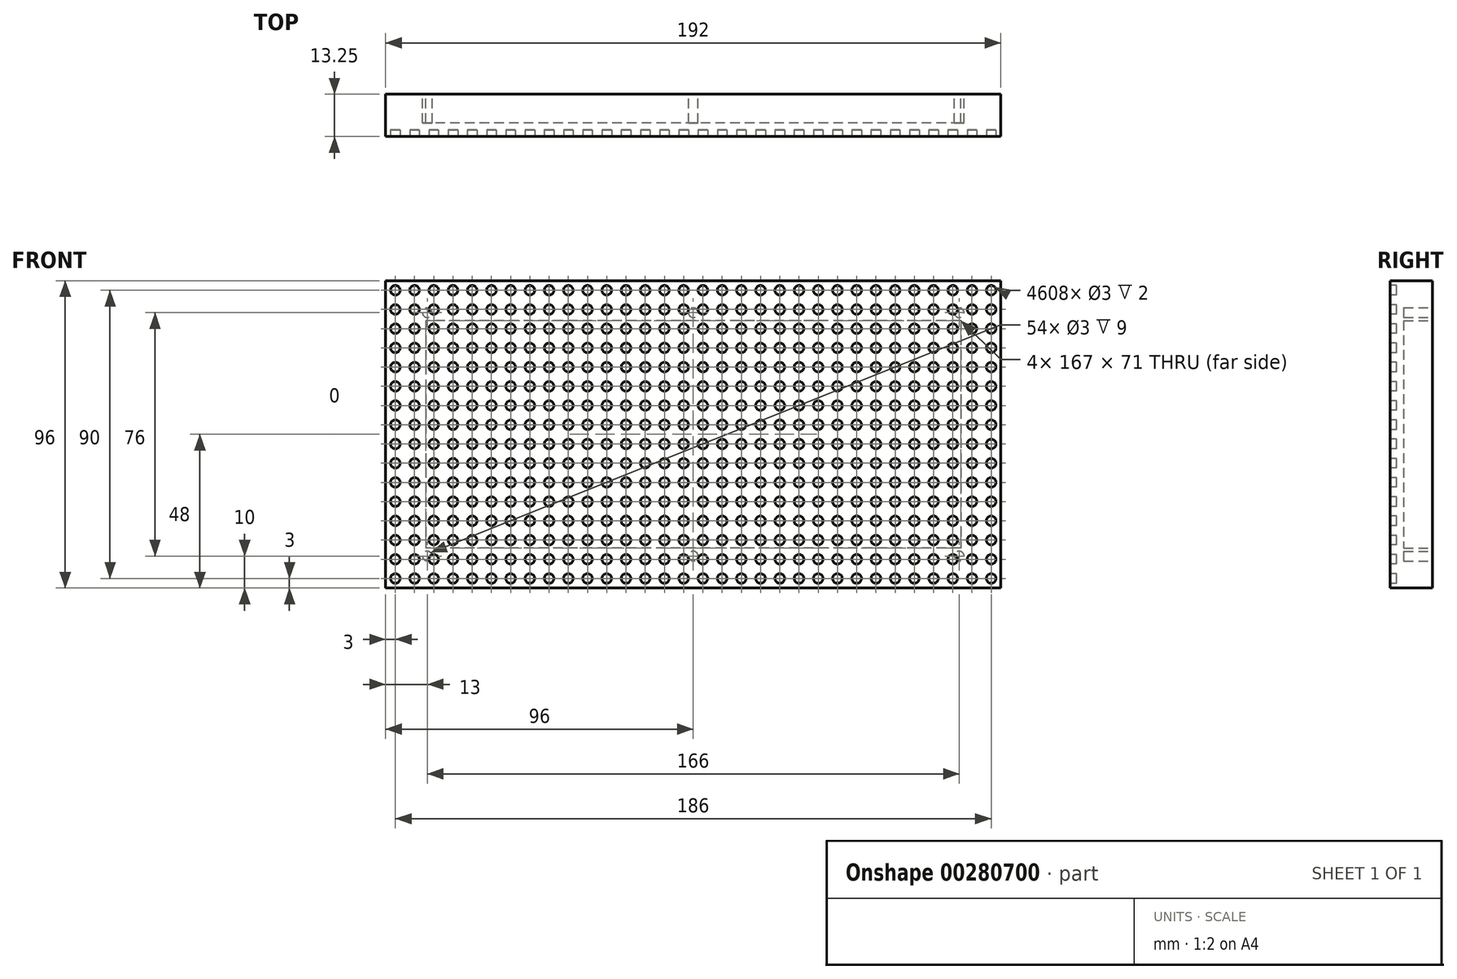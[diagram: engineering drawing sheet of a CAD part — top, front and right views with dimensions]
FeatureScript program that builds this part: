
annotation { "Feature Type Name" : "Feature", "Feature Type Description" : "" }
export const myFeature = defineFeature(function(context is Context, id is Id, definition is map)
    precondition{}
    {
        {
            var Q0;
            Q0=qCreatedBy(makeId("Front.planeOp"),FACE);
            var sketch = newSketch(context, id + "F0", { "sketchPlane" : qUnion([Q0])});
            skLineSegment(sketch, "E0.bottom", {"start": v(0, 0) * mm, "end": v(192, 0) * mm});
            skLineSegment(sketch, "E0.top", {"start": v(0, 96) * mm, "end": v(192, 96) * mm});
            skLineSegment(sketch, "E0.left", {"start": v(0, 0) * mm, "end": v(0, 96) * mm});
            skLineSegment(sketch, "E0.right", {"start": v(192, 0) * mm, "end": v(192, 96) * mm});
            skSolve(sketch);
        }
        {
            var Q0;
            Q0 = qSketchRegion(id + "F0", true);
            extrude(context, id + "F1", {"entities" : qUnion([Q0]), "depth" : 13.25 * mm});
        }
        {
            var Q0;
            Q0=makeQuery(id+"F1.opExtrude","CAP_FACE",FACE,{"disambiguationData":[OSD([sQuery(id+"F0.wireOp",EDGE,"E0.bottom"),sQuery(id+"F0.wireOp",EDGE,"E0.top"),sQuery(id+"F0.wireOp",EDGE,"E0.left"),sQuery(id+"F0.wireOp",EDGE,"E0.right")])],"isStart":true});
            var sketch = newSketch(context, id + "F2", { "sketchPlane" : qUnion([Q0])});
            skLineSegment(sketch, "E1.bottom", {"start": v(-179.5, 83.5) * mm, "end": v(-12.5, 83.5) * mm});
            skLineSegment(sketch, "E1.top", {"start": v(-179.5, 12.5) * mm, "end": v(-12.5, 12.5) * mm});
            skLineSegment(sketch, "E1.left", {"start": v(-179.5, 83.5) * mm, "end": v(-179.5, 12.5) * mm});
            skLineSegment(sketch, "E1.right", {"start": v(-12.5, 83.5) * mm, "end": v(-12.5, 12.5) * mm});
            skSolve(sketch);
        }
        {
            var Q0;
            Q0 = qSketchRegion(id + "F2", true);
            extrude(context, id + "F3", {"entities" : qUnion([Q0]), "operationType" : NewBodyOperationType.REMOVE, "oppositeDirection" : true, "depth" : 9 * mm});
        }
        {
            var Q0;
            Q0=makeQuery(id+"F1.opExtrude","CAP_FACE",FACE,{"disambiguationData":[OSD([sQuery(id+"F0.wireOp",EDGE,"E0.bottom"),sQuery(id+"F0.wireOp",EDGE,"E0.top"),sQuery(id+"F0.wireOp",EDGE,"E0.left"),sQuery(id+"F0.wireOp",EDGE,"E0.right")])],"isStart":true});
            var sketch = newSketch(context, id + "F4", { "sketchPlane" : qUnion([Q0])});
            skCircle(sketch, "E2", {"center": v(-179, 86) * mm, "radius": 1.5 * mm});
            skCircle(sketch, "E3", {"center": v(-96, 86) * mm, "radius": 1.5 * mm});
            skCircle(sketch, "E4", {"center": v(-13, 86) * mm, "radius": 1.5 * mm});
            skCircle(sketch, "E5", {"center": v(-179, 10) * mm, "radius": 1.5 * mm});
            skCircle(sketch, "E6", {"center": v(-96, 10) * mm, "radius": 1.5 * mm});
            skCircle(sketch, "E7", {"center": v(-13, 10) * mm, "radius": 1.5 * mm});
            skSolve(sketch);
        }
        {
            var Q0;
            Q0 = qSketchRegion(id + "F4", true);
            extrude(context, id + "F5", {"entities" : qUnion([Q0]), "operationType" : NewBodyOperationType.REMOVE, "oppositeDirection" : true, "depth" : 9 * mm});
        }
        {
            var Q0;
            Q0 = qSketchRegion(id + "F4", true);
            extrude(context, id + "F6", {"entities" : qUnion([Q0]), "operationType" : NewBodyOperationType.REMOVE, "oppositeDirection" : true, "depth" : 9 * mm});
        }
        {
            var Q0;
            Q0=makeQuery(id+"F1.opExtrude","CAP_FACE",FACE,{"disambiguationData":[OSD([sQuery(id+"F0.wireOp",EDGE,"E0.bottom"),sQuery(id+"F0.wireOp",EDGE,"E0.top"),sQuery(id+"F0.wireOp",EDGE,"E0.left"),sQuery(id+"F0.wireOp",EDGE,"E0.right")])],"isStart":false});
            var sketch = newSketch(context, id + "F7", { "sketchPlane" : qUnion([Q0])});
            skCircle(sketch, "E8", {"center": v(3, 3) * mm, "radius": 1.5 * mm});
            skCircle(sketch, "E9.0.1.0", {"center": v(3, 9) * mm, "radius": 1.5 * mm});
            skCircle(sketch, "E9.0.2.0", {"center": v(3, 15) * mm, "radius": 1.5 * mm});
            skCircle(sketch, "E9.0.3.0", {"center": v(3, 21) * mm, "radius": 1.5 * mm});
            skCircle(sketch, "E9.0.4.0", {"center": v(3, 27) * mm, "radius": 1.5 * mm});
            skCircle(sketch, "E9.0.5.0", {"center": v(3, 33) * mm, "radius": 1.5 * mm});
            skCircle(sketch, "E9.0.6.0", {"center": v(3, 39) * mm, "radius": 1.5 * mm});
            skCircle(sketch, "E9.0.7.0", {"center": v(3, 45) * mm, "radius": 1.5 * mm});
            skCircle(sketch, "E9.0.8.0", {"center": v(3, 51) * mm, "radius": 1.5 * mm});
            skCircle(sketch, "E9.0.9.0", {"center": v(3, 57) * mm, "radius": 1.5 * mm});
            skCircle(sketch, "E9.0.10.0", {"center": v(3, 63) * mm, "radius": 1.5 * mm});
            skCircle(sketch, "E9.0.11.0", {"center": v(3, 69) * mm, "radius": 1.5 * mm});
            skCircle(sketch, "E9.0.12.0", {"center": v(3, 75) * mm, "radius": 1.5 * mm});
            skCircle(sketch, "E9.0.13.0", {"center": v(3, 81) * mm, "radius": 1.5 * mm});
            skCircle(sketch, "E9.0.14.0", {"center": v(3, 87) * mm, "radius": 1.5 * mm});
            skCircle(sketch, "E9.0.15.0", {"center": v(3, 93) * mm, "radius": 1.5 * mm});
            skCircle(sketch, "E9.1.0.0", {"center": v(9, 3) * mm, "radius": 1.5 * mm});
            skCircle(sketch, "E9.1.1.0", {"center": v(9, 9) * mm, "radius": 1.5 * mm});
            skCircle(sketch, "E9.1.2.0", {"center": v(9, 15) * mm, "radius": 1.5 * mm});
            skCircle(sketch, "E9.1.3.0", {"center": v(9, 21) * mm, "radius": 1.5 * mm});
            skCircle(sketch, "E9.1.4.0", {"center": v(9, 27) * mm, "radius": 1.5 * mm});
            skCircle(sketch, "E9.1.5.0", {"center": v(9, 33) * mm, "radius": 1.5 * mm});
            skCircle(sketch, "E9.1.6.0", {"center": v(9, 39) * mm, "radius": 1.5 * mm});
            skCircle(sketch, "E9.1.7.0", {"center": v(9, 45) * mm, "radius": 1.5 * mm});
            skCircle(sketch, "E9.1.8.0", {"center": v(9, 51) * mm, "radius": 1.5 * mm});
            skCircle(sketch, "E9.1.9.0", {"center": v(9, 57) * mm, "radius": 1.5 * mm});
            skCircle(sketch, "E9.1.10.0", {"center": v(9, 63) * mm, "radius": 1.5 * mm});
            skCircle(sketch, "E9.1.11.0", {"center": v(9, 69) * mm, "radius": 1.5 * mm});
            skCircle(sketch, "E9.1.12.0", {"center": v(9, 75) * mm, "radius": 1.5 * mm});
            skCircle(sketch, "E9.1.13.0", {"center": v(9, 81) * mm, "radius": 1.5 * mm});
            skCircle(sketch, "E9.1.14.0", {"center": v(9, 87) * mm, "radius": 1.5 * mm});
            skCircle(sketch, "E9.1.15.0", {"center": v(9, 93) * mm, "radius": 1.5 * mm});
            skCircle(sketch, "E9.2.0.0", {"center": v(15, 3) * mm, "radius": 1.5 * mm});
            skCircle(sketch, "E9.2.1.0", {"center": v(15, 9) * mm, "radius": 1.5 * mm});
            skCircle(sketch, "E9.2.2.0", {"center": v(15, 15) * mm, "radius": 1.5 * mm});
            skCircle(sketch, "E9.2.3.0", {"center": v(15, 21) * mm, "radius": 1.5 * mm});
            skCircle(sketch, "E9.2.4.0", {"center": v(15, 27) * mm, "radius": 1.5 * mm});
            skCircle(sketch, "E9.2.5.0", {"center": v(15, 33) * mm, "radius": 1.5 * mm});
            skCircle(sketch, "E9.2.6.0", {"center": v(15, 39) * mm, "radius": 1.5 * mm});
            skCircle(sketch, "E9.2.7.0", {"center": v(15, 45) * mm, "radius": 1.5 * mm});
            skCircle(sketch, "E9.2.8.0", {"center": v(15, 51) * mm, "radius": 1.5 * mm});
            skCircle(sketch, "E9.2.9.0", {"center": v(15, 57) * mm, "radius": 1.5 * mm});
            skCircle(sketch, "E9.2.10.0", {"center": v(15, 63) * mm, "radius": 1.5 * mm});
            skCircle(sketch, "E9.2.11.0", {"center": v(15, 69) * mm, "radius": 1.5 * mm});
            skCircle(sketch, "E9.2.12.0", {"center": v(15, 75) * mm, "radius": 1.5 * mm});
            skCircle(sketch, "E9.2.13.0", {"center": v(15, 81) * mm, "radius": 1.5 * mm});
            skCircle(sketch, "E9.2.14.0", {"center": v(15, 87) * mm, "radius": 1.5 * mm});
            skCircle(sketch, "E9.2.15.0", {"center": v(15, 93) * mm, "radius": 1.5 * mm});
            skCircle(sketch, "E9.3.0.0", {"center": v(21, 3) * mm, "radius": 1.5 * mm});
            skCircle(sketch, "E9.3.1.0", {"center": v(21, 9) * mm, "radius": 1.5 * mm});
            skCircle(sketch, "E9.3.2.0", {"center": v(21, 15) * mm, "radius": 1.5 * mm});
            skCircle(sketch, "E9.3.3.0", {"center": v(21, 21) * mm, "radius": 1.5 * mm});
            skCircle(sketch, "E9.3.4.0", {"center": v(21, 27) * mm, "radius": 1.5 * mm});
            skCircle(sketch, "E9.3.5.0", {"center": v(21, 33) * mm, "radius": 1.5 * mm});
            skCircle(sketch, "E9.3.6.0", {"center": v(21, 39) * mm, "radius": 1.5 * mm});
            skCircle(sketch, "E9.3.7.0", {"center": v(21, 45) * mm, "radius": 1.5 * mm});
            skCircle(sketch, "E9.3.8.0", {"center": v(21, 51) * mm, "radius": 1.5 * mm});
            skCircle(sketch, "E9.3.9.0", {"center": v(21, 57) * mm, "radius": 1.5 * mm});
            skCircle(sketch, "E9.3.10.0", {"center": v(21, 63) * mm, "radius": 1.5 * mm});
            skCircle(sketch, "E9.3.11.0", {"center": v(21, 69) * mm, "radius": 1.5 * mm});
            skCircle(sketch, "E9.3.12.0", {"center": v(21, 75) * mm, "radius": 1.5 * mm});
            skCircle(sketch, "E9.3.13.0", {"center": v(21, 81) * mm, "radius": 1.5 * mm});
            skCircle(sketch, "E9.3.14.0", {"center": v(21, 87) * mm, "radius": 1.5 * mm});
            skCircle(sketch, "E9.3.15.0", {"center": v(21, 93) * mm, "radius": 1.5 * mm});
            skCircle(sketch, "E9.4.0.0", {"center": v(27, 3) * mm, "radius": 1.5 * mm});
            skCircle(sketch, "E9.4.1.0", {"center": v(27, 9) * mm, "radius": 1.5 * mm});
            skCircle(sketch, "E9.4.2.0", {"center": v(27, 15) * mm, "radius": 1.5 * mm});
            skCircle(sketch, "E9.4.3.0", {"center": v(27, 21) * mm, "radius": 1.5 * mm});
            skCircle(sketch, "E9.4.4.0", {"center": v(27, 27) * mm, "radius": 1.5 * mm});
            skCircle(sketch, "E9.4.5.0", {"center": v(27, 33) * mm, "radius": 1.5 * mm});
            skCircle(sketch, "E9.4.6.0", {"center": v(27, 39) * mm, "radius": 1.5 * mm});
            skCircle(sketch, "E9.4.7.0", {"center": v(27, 45) * mm, "radius": 1.5 * mm});
            skCircle(sketch, "E9.4.8.0", {"center": v(27, 51) * mm, "radius": 1.5 * mm});
            skCircle(sketch, "E9.4.9.0", {"center": v(27, 57) * mm, "radius": 1.5 * mm});
            skCircle(sketch, "E9.4.10.0", {"center": v(27, 63) * mm, "radius": 1.5 * mm});
            skCircle(sketch, "E9.4.11.0", {"center": v(27, 69) * mm, "radius": 1.5 * mm});
            skCircle(sketch, "E9.4.12.0", {"center": v(27, 75) * mm, "radius": 1.5 * mm});
            skCircle(sketch, "E9.4.13.0", {"center": v(27, 81) * mm, "radius": 1.5 * mm});
            skCircle(sketch, "E9.4.14.0", {"center": v(27, 87) * mm, "radius": 1.5 * mm});
            skCircle(sketch, "E9.4.15.0", {"center": v(27, 93) * mm, "radius": 1.5 * mm});
            skCircle(sketch, "E9.5.0.0", {"center": v(33, 3) * mm, "radius": 1.5 * mm});
            skCircle(sketch, "E9.5.1.0", {"center": v(33, 9) * mm, "radius": 1.5 * mm});
            skCircle(sketch, "E9.5.2.0", {"center": v(33, 15) * mm, "radius": 1.5 * mm});
            skCircle(sketch, "E9.5.3.0", {"center": v(33, 21) * mm, "radius": 1.5 * mm});
            skCircle(sketch, "E9.5.4.0", {"center": v(33, 27) * mm, "radius": 1.5 * mm});
            skCircle(sketch, "E9.5.5.0", {"center": v(33, 33) * mm, "radius": 1.5 * mm});
            skCircle(sketch, "E9.5.6.0", {"center": v(33, 39) * mm, "radius": 1.5 * mm});
            skCircle(sketch, "E9.5.7.0", {"center": v(33, 45) * mm, "radius": 1.5 * mm});
            skCircle(sketch, "E9.5.8.0", {"center": v(33, 51) * mm, "radius": 1.5 * mm});
            skCircle(sketch, "E9.5.9.0", {"center": v(33, 57) * mm, "radius": 1.5 * mm});
            skCircle(sketch, "E9.5.10.0", {"center": v(33, 63) * mm, "radius": 1.5 * mm});
            skCircle(sketch, "E9.5.11.0", {"center": v(33, 69) * mm, "radius": 1.5 * mm});
            skCircle(sketch, "E9.5.12.0", {"center": v(33, 75) * mm, "radius": 1.5 * mm});
            skCircle(sketch, "E9.5.13.0", {"center": v(33, 81) * mm, "radius": 1.5 * mm});
            skCircle(sketch, "E9.5.14.0", {"center": v(33, 87) * mm, "radius": 1.5 * mm});
            skCircle(sketch, "E9.5.15.0", {"center": v(33, 93) * mm, "radius": 1.5 * mm});
            skCircle(sketch, "E9.6.0.0", {"center": v(39, 3) * mm, "radius": 1.5 * mm});
            skCircle(sketch, "E9.6.1.0", {"center": v(39, 9) * mm, "radius": 1.5 * mm});
            skCircle(sketch, "E9.6.2.0", {"center": v(39, 15) * mm, "radius": 1.5 * mm});
            skCircle(sketch, "E9.6.3.0", {"center": v(39, 21) * mm, "radius": 1.5 * mm});
            skCircle(sketch, "E9.6.4.0", {"center": v(39, 27) * mm, "radius": 1.5 * mm});
            skCircle(sketch, "E9.6.5.0", {"center": v(39, 33) * mm, "radius": 1.5 * mm});
            skCircle(sketch, "E9.6.6.0", {"center": v(39, 39) * mm, "radius": 1.5 * mm});
            skCircle(sketch, "E9.6.7.0", {"center": v(39, 45) * mm, "radius": 1.5 * mm});
            skCircle(sketch, "E9.6.8.0", {"center": v(39, 51) * mm, "radius": 1.5 * mm});
            skCircle(sketch, "E9.6.9.0", {"center": v(39, 57) * mm, "radius": 1.5 * mm});
            skCircle(sketch, "E9.6.10.0", {"center": v(39, 63) * mm, "radius": 1.5 * mm});
            skCircle(sketch, "E9.6.11.0", {"center": v(39, 69) * mm, "radius": 1.5 * mm});
            skCircle(sketch, "E9.6.12.0", {"center": v(39, 75) * mm, "radius": 1.5 * mm});
            skCircle(sketch, "E9.6.13.0", {"center": v(39, 81) * mm, "radius": 1.5 * mm});
            skCircle(sketch, "E9.6.14.0", {"center": v(39, 87) * mm, "radius": 1.5 * mm});
            skCircle(sketch, "E9.6.15.0", {"center": v(39, 93) * mm, "radius": 1.5 * mm});
            skCircle(sketch, "E9.7.0.0", {"center": v(45, 3) * mm, "radius": 1.5 * mm});
            skCircle(sketch, "E9.7.1.0", {"center": v(45, 9) * mm, "radius": 1.5 * mm});
            skCircle(sketch, "E9.7.2.0", {"center": v(45, 15) * mm, "radius": 1.5 * mm});
            skCircle(sketch, "E9.7.3.0", {"center": v(45, 21) * mm, "radius": 1.5 * mm});
            skCircle(sketch, "E9.7.4.0", {"center": v(45, 27) * mm, "radius": 1.5 * mm});
            skCircle(sketch, "E9.7.5.0", {"center": v(45, 33) * mm, "radius": 1.5 * mm});
            skCircle(sketch, "E9.7.6.0", {"center": v(45, 39) * mm, "radius": 1.5 * mm});
            skCircle(sketch, "E9.7.7.0", {"center": v(45, 45) * mm, "radius": 1.5 * mm});
            skCircle(sketch, "E9.7.8.0", {"center": v(45, 51) * mm, "radius": 1.5 * mm});
            skCircle(sketch, "E9.7.9.0", {"center": v(45, 57) * mm, "radius": 1.5 * mm});
            skCircle(sketch, "E9.7.10.0", {"center": v(45, 63) * mm, "radius": 1.5 * mm});
            skCircle(sketch, "E9.7.11.0", {"center": v(45, 69) * mm, "radius": 1.5 * mm});
            skCircle(sketch, "E9.7.12.0", {"center": v(45, 75) * mm, "radius": 1.5 * mm});
            skCircle(sketch, "E9.7.13.0", {"center": v(45, 81) * mm, "radius": 1.5 * mm});
            skCircle(sketch, "E9.7.14.0", {"center": v(45, 87) * mm, "radius": 1.5 * mm});
            skCircle(sketch, "E9.7.15.0", {"center": v(45, 93) * mm, "radius": 1.5 * mm});
            skCircle(sketch, "E9.8.0.0", {"center": v(51, 3) * mm, "radius": 1.5 * mm});
            skCircle(sketch, "E9.8.1.0", {"center": v(51, 9) * mm, "radius": 1.5 * mm});
            skCircle(sketch, "E9.8.2.0", {"center": v(51, 15) * mm, "radius": 1.5 * mm});
            skCircle(sketch, "E9.8.3.0", {"center": v(51, 21) * mm, "radius": 1.5 * mm});
            skCircle(sketch, "E9.8.4.0", {"center": v(51, 27) * mm, "radius": 1.5 * mm});
            skCircle(sketch, "E9.8.5.0", {"center": v(51, 33) * mm, "radius": 1.5 * mm});
            skCircle(sketch, "E9.8.6.0", {"center": v(51, 39) * mm, "radius": 1.5 * mm});
            skCircle(sketch, "E9.8.7.0", {"center": v(51, 45) * mm, "radius": 1.5 * mm});
            skCircle(sketch, "E9.8.8.0", {"center": v(51, 51) * mm, "radius": 1.5 * mm});
            skCircle(sketch, "E9.8.9.0", {"center": v(51, 57) * mm, "radius": 1.5 * mm});
            skCircle(sketch, "E9.8.10.0", {"center": v(51, 63) * mm, "radius": 1.5 * mm});
            skCircle(sketch, "E9.8.11.0", {"center": v(51, 69) * mm, "radius": 1.5 * mm});
            skCircle(sketch, "E9.8.12.0", {"center": v(51, 75) * mm, "radius": 1.5 * mm});
            skCircle(sketch, "E9.8.13.0", {"center": v(51, 81) * mm, "radius": 1.5 * mm});
            skCircle(sketch, "E9.8.14.0", {"center": v(51, 87) * mm, "radius": 1.5 * mm});
            skCircle(sketch, "E9.8.15.0", {"center": v(51, 93) * mm, "radius": 1.5 * mm});
            skCircle(sketch, "E9.9.0.0", {"center": v(57, 3) * mm, "radius": 1.5 * mm});
            skCircle(sketch, "E9.9.1.0", {"center": v(57, 9) * mm, "radius": 1.5 * mm});
            skCircle(sketch, "E9.9.2.0", {"center": v(57, 15) * mm, "radius": 1.5 * mm});
            skCircle(sketch, "E9.9.3.0", {"center": v(57, 21) * mm, "radius": 1.5 * mm});
            skCircle(sketch, "E9.9.4.0", {"center": v(57, 27) * mm, "radius": 1.5 * mm});
            skCircle(sketch, "E9.9.5.0", {"center": v(57, 33) * mm, "radius": 1.5 * mm});
            skCircle(sketch, "E9.9.6.0", {"center": v(57, 39) * mm, "radius": 1.5 * mm});
            skCircle(sketch, "E9.9.7.0", {"center": v(57, 45) * mm, "radius": 1.5 * mm});
            skCircle(sketch, "E9.9.8.0", {"center": v(57, 51) * mm, "radius": 1.5 * mm});
            skCircle(sketch, "E9.9.9.0", {"center": v(57, 57) * mm, "radius": 1.5 * mm});
            skCircle(sketch, "E9.9.10.0", {"center": v(57, 63) * mm, "radius": 1.5 * mm});
            skCircle(sketch, "E9.9.11.0", {"center": v(57, 69) * mm, "radius": 1.5 * mm});
            skCircle(sketch, "E9.9.12.0", {"center": v(57, 75) * mm, "radius": 1.5 * mm});
            skCircle(sketch, "E9.9.13.0", {"center": v(57, 81) * mm, "radius": 1.5 * mm});
            skCircle(sketch, "E9.9.14.0", {"center": v(57, 87) * mm, "radius": 1.5 * mm});
            skCircle(sketch, "E9.9.15.0", {"center": v(57, 93) * mm, "radius": 1.5 * mm});
            skCircle(sketch, "E9.10.0.0", {"center": v(63, 3) * mm, "radius": 1.5 * mm});
            skCircle(sketch, "E9.10.1.0", {"center": v(63, 9) * mm, "radius": 1.5 * mm});
            skCircle(sketch, "E9.10.2.0", {"center": v(63, 15) * mm, "radius": 1.5 * mm});
            skCircle(sketch, "E9.10.3.0", {"center": v(63, 21) * mm, "radius": 1.5 * mm});
            skCircle(sketch, "E9.10.4.0", {"center": v(63, 27) * mm, "radius": 1.5 * mm});
            skCircle(sketch, "E9.10.5.0", {"center": v(63, 33) * mm, "radius": 1.5 * mm});
            skCircle(sketch, "E9.10.6.0", {"center": v(63, 39) * mm, "radius": 1.5 * mm});
            skCircle(sketch, "E9.10.7.0", {"center": v(63, 45) * mm, "radius": 1.5 * mm});
            skCircle(sketch, "E9.10.8.0", {"center": v(63, 51) * mm, "radius": 1.5 * mm});
            skCircle(sketch, "E9.10.9.0", {"center": v(63, 57) * mm, "radius": 1.5 * mm});
            skCircle(sketch, "E9.10.10.0", {"center": v(63, 63) * mm, "radius": 1.5 * mm});
            skCircle(sketch, "E9.10.11.0", {"center": v(63, 69) * mm, "radius": 1.5 * mm});
            skCircle(sketch, "E9.10.12.0", {"center": v(63, 75) * mm, "radius": 1.5 * mm});
            skCircle(sketch, "E9.10.13.0", {"center": v(63, 81) * mm, "radius": 1.5 * mm});
            skCircle(sketch, "E9.10.14.0", {"center": v(63, 87) * mm, "radius": 1.5 * mm});
            skCircle(sketch, "E9.10.15.0", {"center": v(63, 93) * mm, "radius": 1.5 * mm});
            skCircle(sketch, "E9.11.0.0", {"center": v(69, 3) * mm, "radius": 1.5 * mm});
            skCircle(sketch, "E9.11.1.0", {"center": v(69, 9) * mm, "radius": 1.5 * mm});
            skCircle(sketch, "E9.11.2.0", {"center": v(69, 15) * mm, "radius": 1.5 * mm});
            skCircle(sketch, "E9.11.3.0", {"center": v(69, 21) * mm, "radius": 1.5 * mm});
            skCircle(sketch, "E9.11.4.0", {"center": v(69, 27) * mm, "radius": 1.5 * mm});
            skCircle(sketch, "E9.11.5.0", {"center": v(69, 33) * mm, "radius": 1.5 * mm});
            skCircle(sketch, "E9.11.6.0", {"center": v(69, 39) * mm, "radius": 1.5 * mm});
            skCircle(sketch, "E9.11.7.0", {"center": v(69, 45) * mm, "radius": 1.5 * mm});
            skCircle(sketch, "E9.11.8.0", {"center": v(69, 51) * mm, "radius": 1.5 * mm});
            skCircle(sketch, "E9.11.9.0", {"center": v(69, 57) * mm, "radius": 1.5 * mm});
            skCircle(sketch, "E9.11.10.0", {"center": v(69, 63) * mm, "radius": 1.5 * mm});
            skCircle(sketch, "E9.11.11.0", {"center": v(69, 69) * mm, "radius": 1.5 * mm});
            skCircle(sketch, "E9.11.12.0", {"center": v(69, 75) * mm, "radius": 1.5 * mm});
            skCircle(sketch, "E9.11.13.0", {"center": v(69, 81) * mm, "radius": 1.5 * mm});
            skCircle(sketch, "E9.11.14.0", {"center": v(69, 87) * mm, "radius": 1.5 * mm});
            skCircle(sketch, "E9.11.15.0", {"center": v(69, 93) * mm, "radius": 1.5 * mm});
            skCircle(sketch, "E9.12.0.0", {"center": v(75, 3) * mm, "radius": 1.5 * mm});
            skCircle(sketch, "E9.12.1.0", {"center": v(75, 9) * mm, "radius": 1.5 * mm});
            skCircle(sketch, "E9.12.2.0", {"center": v(75, 15) * mm, "radius": 1.5 * mm});
            skCircle(sketch, "E9.12.3.0", {"center": v(75, 21) * mm, "radius": 1.5 * mm});
            skCircle(sketch, "E9.12.4.0", {"center": v(75, 27) * mm, "radius": 1.5 * mm});
            skCircle(sketch, "E9.12.5.0", {"center": v(75, 33) * mm, "radius": 1.5 * mm});
            skCircle(sketch, "E9.12.6.0", {"center": v(75, 39) * mm, "radius": 1.5 * mm});
            skCircle(sketch, "E9.12.7.0", {"center": v(75, 45) * mm, "radius": 1.5 * mm});
            skCircle(sketch, "E9.12.8.0", {"center": v(75, 51) * mm, "radius": 1.5 * mm});
            skCircle(sketch, "E9.12.9.0", {"center": v(75, 57) * mm, "radius": 1.5 * mm});
            skCircle(sketch, "E9.12.10.0", {"center": v(75, 63) * mm, "radius": 1.5 * mm});
            skCircle(sketch, "E9.12.11.0", {"center": v(75, 69) * mm, "radius": 1.5 * mm});
            skCircle(sketch, "E9.12.12.0", {"center": v(75, 75) * mm, "radius": 1.5 * mm});
            skCircle(sketch, "E9.12.13.0", {"center": v(75, 81) * mm, "radius": 1.5 * mm});
            skCircle(sketch, "E9.12.14.0", {"center": v(75, 87) * mm, "radius": 1.5 * mm});
            skCircle(sketch, "E9.12.15.0", {"center": v(75, 93) * mm, "radius": 1.5 * mm});
            skCircle(sketch, "E9.13.0.0", {"center": v(81, 3) * mm, "radius": 1.5 * mm});
            skCircle(sketch, "E9.13.1.0", {"center": v(81, 9) * mm, "radius": 1.5 * mm});
            skCircle(sketch, "E9.13.2.0", {"center": v(81, 15) * mm, "radius": 1.5 * mm});
            skCircle(sketch, "E9.13.3.0", {"center": v(81, 21) * mm, "radius": 1.5 * mm});
            skCircle(sketch, "E9.13.4.0", {"center": v(81, 27) * mm, "radius": 1.5 * mm});
            skCircle(sketch, "E9.13.5.0", {"center": v(81, 33) * mm, "radius": 1.5 * mm});
            skCircle(sketch, "E9.13.6.0", {"center": v(81, 39) * mm, "radius": 1.5 * mm});
            skCircle(sketch, "E9.13.7.0", {"center": v(81, 45) * mm, "radius": 1.5 * mm});
            skCircle(sketch, "E9.13.8.0", {"center": v(81, 51) * mm, "radius": 1.5 * mm});
            skCircle(sketch, "E9.13.9.0", {"center": v(81, 57) * mm, "radius": 1.5 * mm});
            skCircle(sketch, "E9.13.10.0", {"center": v(81, 63) * mm, "radius": 1.5 * mm});
            skCircle(sketch, "E9.13.11.0", {"center": v(81, 69) * mm, "radius": 1.5 * mm});
            skCircle(sketch, "E9.13.12.0", {"center": v(81, 75) * mm, "radius": 1.5 * mm});
            skCircle(sketch, "E9.13.13.0", {"center": v(81, 81) * mm, "radius": 1.5 * mm});
            skCircle(sketch, "E9.13.14.0", {"center": v(81, 87) * mm, "radius": 1.5 * mm});
            skCircle(sketch, "E9.13.15.0", {"center": v(81, 93) * mm, "radius": 1.5 * mm});
            skCircle(sketch, "E9.14.0.0", {"center": v(87, 3) * mm, "radius": 1.5 * mm});
            skCircle(sketch, "E9.14.1.0", {"center": v(87, 9) * mm, "radius": 1.5 * mm});
            skCircle(sketch, "E9.14.2.0", {"center": v(87, 15) * mm, "radius": 1.5 * mm});
            skCircle(sketch, "E9.14.3.0", {"center": v(87, 21) * mm, "radius": 1.5 * mm});
            skCircle(sketch, "E9.14.4.0", {"center": v(87, 27) * mm, "radius": 1.5 * mm});
            skCircle(sketch, "E9.14.5.0", {"center": v(87, 33) * mm, "radius": 1.5 * mm});
            skCircle(sketch, "E9.14.6.0", {"center": v(87, 39) * mm, "radius": 1.5 * mm});
            skCircle(sketch, "E9.14.7.0", {"center": v(87, 45) * mm, "radius": 1.5 * mm});
            skCircle(sketch, "E9.14.8.0", {"center": v(87, 51) * mm, "radius": 1.5 * mm});
            skCircle(sketch, "E9.14.9.0", {"center": v(87, 57) * mm, "radius": 1.5 * mm});
            skCircle(sketch, "E9.14.10.0", {"center": v(87, 63) * mm, "radius": 1.5 * mm});
            skCircle(sketch, "E9.14.11.0", {"center": v(87, 69) * mm, "radius": 1.5 * mm});
            skCircle(sketch, "E9.14.12.0", {"center": v(87, 75) * mm, "radius": 1.5 * mm});
            skCircle(sketch, "E9.14.13.0", {"center": v(87, 81) * mm, "radius": 1.5 * mm});
            skCircle(sketch, "E9.14.14.0", {"center": v(87, 87) * mm, "radius": 1.5 * mm});
            skCircle(sketch, "E9.14.15.0", {"center": v(87, 93) * mm, "radius": 1.5 * mm});
            skCircle(sketch, "E9.15.0.0", {"center": v(93, 3) * mm, "radius": 1.5 * mm});
            skCircle(sketch, "E9.15.1.0", {"center": v(93, 9) * mm, "radius": 1.5 * mm});
            skCircle(sketch, "E9.15.2.0", {"center": v(93, 15) * mm, "radius": 1.5 * mm});
            skCircle(sketch, "E9.15.3.0", {"center": v(93, 21) * mm, "radius": 1.5 * mm});
            skCircle(sketch, "E9.15.4.0", {"center": v(93, 27) * mm, "radius": 1.5 * mm});
            skCircle(sketch, "E9.15.5.0", {"center": v(93, 33) * mm, "radius": 1.5 * mm});
            skCircle(sketch, "E9.15.6.0", {"center": v(93, 39) * mm, "radius": 1.5 * mm});
            skCircle(sketch, "E9.15.7.0", {"center": v(93, 45) * mm, "radius": 1.5 * mm});
            skCircle(sketch, "E9.15.8.0", {"center": v(93, 51) * mm, "radius": 1.5 * mm});
            skCircle(sketch, "E9.15.9.0", {"center": v(93, 57) * mm, "radius": 1.5 * mm});
            skCircle(sketch, "E9.15.10.0", {"center": v(93, 63) * mm, "radius": 1.5 * mm});
            skCircle(sketch, "E9.15.11.0", {"center": v(93, 69) * mm, "radius": 1.5 * mm});
            skCircle(sketch, "E9.15.12.0", {"center": v(93, 75) * mm, "radius": 1.5 * mm});
            skCircle(sketch, "E9.15.13.0", {"center": v(93, 81) * mm, "radius": 1.5 * mm});
            skCircle(sketch, "E9.15.14.0", {"center": v(93, 87) * mm, "radius": 1.5 * mm});
            skCircle(sketch, "E9.15.15.0", {"center": v(93, 93) * mm, "radius": 1.5 * mm});
            skCircle(sketch, "E9.16.0.0", {"center": v(99, 3) * mm, "radius": 1.5 * mm});
            skCircle(sketch, "E9.16.1.0", {"center": v(99, 9) * mm, "radius": 1.5 * mm});
            skCircle(sketch, "E9.16.2.0", {"center": v(99, 15) * mm, "radius": 1.5 * mm});
            skCircle(sketch, "E9.16.3.0", {"center": v(99, 21) * mm, "radius": 1.5 * mm});
            skCircle(sketch, "E9.16.4.0", {"center": v(99, 27) * mm, "radius": 1.5 * mm});
            skCircle(sketch, "E9.16.5.0", {"center": v(99, 33) * mm, "radius": 1.5 * mm});
            skCircle(sketch, "E9.16.6.0", {"center": v(99, 39) * mm, "radius": 1.5 * mm});
            skCircle(sketch, "E9.16.7.0", {"center": v(99, 45) * mm, "radius": 1.5 * mm});
            skCircle(sketch, "E9.16.8.0", {"center": v(99, 51) * mm, "radius": 1.5 * mm});
            skCircle(sketch, "E9.16.9.0", {"center": v(99, 57) * mm, "radius": 1.5 * mm});
            skCircle(sketch, "E9.16.10.0", {"center": v(99, 63) * mm, "radius": 1.5 * mm});
            skCircle(sketch, "E9.16.11.0", {"center": v(99, 69) * mm, "radius": 1.5 * mm});
            skCircle(sketch, "E9.16.12.0", {"center": v(99, 75) * mm, "radius": 1.5 * mm});
            skCircle(sketch, "E9.16.13.0", {"center": v(99, 81) * mm, "radius": 1.5 * mm});
            skCircle(sketch, "E9.16.14.0", {"center": v(99, 87) * mm, "radius": 1.5 * mm});
            skCircle(sketch, "E9.16.15.0", {"center": v(99, 93) * mm, "radius": 1.5 * mm});
            skCircle(sketch, "E9.17.0.0", {"center": v(105, 3) * mm, "radius": 1.5 * mm});
            skCircle(sketch, "E9.17.1.0", {"center": v(105, 9) * mm, "radius": 1.5 * mm});
            skCircle(sketch, "E9.17.2.0", {"center": v(105, 15) * mm, "radius": 1.5 * mm});
            skCircle(sketch, "E9.17.3.0", {"center": v(105, 21) * mm, "radius": 1.5 * mm});
            skCircle(sketch, "E9.17.4.0", {"center": v(105, 27) * mm, "radius": 1.5 * mm});
            skCircle(sketch, "E9.17.5.0", {"center": v(105, 33) * mm, "radius": 1.5 * mm});
            skCircle(sketch, "E9.17.6.0", {"center": v(105, 39) * mm, "radius": 1.5 * mm});
            skCircle(sketch, "E9.17.7.0", {"center": v(105, 45) * mm, "radius": 1.5 * mm});
            skCircle(sketch, "E9.17.8.0", {"center": v(105, 51) * mm, "radius": 1.5 * mm});
            skCircle(sketch, "E9.17.9.0", {"center": v(105, 57) * mm, "radius": 1.5 * mm});
            skCircle(sketch, "E9.17.10.0", {"center": v(105, 63) * mm, "radius": 1.5 * mm});
            skCircle(sketch, "E9.17.11.0", {"center": v(105, 69) * mm, "radius": 1.5 * mm});
            skCircle(sketch, "E9.17.12.0", {"center": v(105, 75) * mm, "radius": 1.5 * mm});
            skCircle(sketch, "E9.17.13.0", {"center": v(105, 81) * mm, "radius": 1.5 * mm});
            skCircle(sketch, "E9.17.14.0", {"center": v(105, 87) * mm, "radius": 1.5 * mm});
            skCircle(sketch, "E9.17.15.0", {"center": v(105, 93) * mm, "radius": 1.5 * mm});
            skCircle(sketch, "E9.18.0.0", {"center": v(111, 3) * mm, "radius": 1.5 * mm});
            skCircle(sketch, "E9.18.1.0", {"center": v(111, 9) * mm, "radius": 1.5 * mm});
            skCircle(sketch, "E9.18.2.0", {"center": v(111, 15) * mm, "radius": 1.5 * mm});
            skCircle(sketch, "E9.18.3.0", {"center": v(111, 21) * mm, "radius": 1.5 * mm});
            skCircle(sketch, "E9.18.4.0", {"center": v(111, 27) * mm, "radius": 1.5 * mm});
            skCircle(sketch, "E9.18.5.0", {"center": v(111, 33) * mm, "radius": 1.5 * mm});
            skCircle(sketch, "E9.18.6.0", {"center": v(111, 39) * mm, "radius": 1.5 * mm});
            skCircle(sketch, "E9.18.7.0", {"center": v(111, 45) * mm, "radius": 1.5 * mm});
            skCircle(sketch, "E9.18.8.0", {"center": v(111, 51) * mm, "radius": 1.5 * mm});
            skCircle(sketch, "E9.18.9.0", {"center": v(111, 57) * mm, "radius": 1.5 * mm});
            skCircle(sketch, "E9.18.10.0", {"center": v(111, 63) * mm, "radius": 1.5 * mm});
            skCircle(sketch, "E9.18.11.0", {"center": v(111, 69) * mm, "radius": 1.5 * mm});
            skCircle(sketch, "E9.18.12.0", {"center": v(111, 75) * mm, "radius": 1.5 * mm});
            skCircle(sketch, "E9.18.13.0", {"center": v(111, 81) * mm, "radius": 1.5 * mm});
            skCircle(sketch, "E9.18.14.0", {"center": v(111, 87) * mm, "radius": 1.5 * mm});
            skCircle(sketch, "E9.18.15.0", {"center": v(111, 93) * mm, "radius": 1.5 * mm});
            skCircle(sketch, "E9.19.0.0", {"center": v(117, 3) * mm, "radius": 1.5 * mm});
            skCircle(sketch, "E9.19.1.0", {"center": v(117, 9) * mm, "radius": 1.5 * mm});
            skCircle(sketch, "E9.19.2.0", {"center": v(117, 15) * mm, "radius": 1.5 * mm});
            skCircle(sketch, "E9.19.3.0", {"center": v(117, 21) * mm, "radius": 1.5 * mm});
            skCircle(sketch, "E9.19.4.0", {"center": v(117, 27) * mm, "radius": 1.5 * mm});
            skCircle(sketch, "E9.19.5.0", {"center": v(117, 33) * mm, "radius": 1.5 * mm});
            skCircle(sketch, "E9.19.6.0", {"center": v(117, 39) * mm, "radius": 1.5 * mm});
            skCircle(sketch, "E9.19.7.0", {"center": v(117, 45) * mm, "radius": 1.5 * mm});
            skCircle(sketch, "E9.19.8.0", {"center": v(117, 51) * mm, "radius": 1.5 * mm});
            skCircle(sketch, "E9.19.9.0", {"center": v(117, 57) * mm, "radius": 1.5 * mm});
            skCircle(sketch, "E9.19.10.0", {"center": v(117, 63) * mm, "radius": 1.5 * mm});
            skCircle(sketch, "E9.19.11.0", {"center": v(117, 69) * mm, "radius": 1.5 * mm});
            skCircle(sketch, "E9.19.12.0", {"center": v(117, 75) * mm, "radius": 1.5 * mm});
            skCircle(sketch, "E9.19.13.0", {"center": v(117, 81) * mm, "radius": 1.5 * mm});
            skCircle(sketch, "E9.19.14.0", {"center": v(117, 87) * mm, "radius": 1.5 * mm});
            skCircle(sketch, "E9.19.15.0", {"center": v(117, 93) * mm, "radius": 1.5 * mm});
            skCircle(sketch, "E9.20.0.0", {"center": v(123, 3) * mm, "radius": 1.5 * mm});
            skCircle(sketch, "E9.20.1.0", {"center": v(123, 9) * mm, "radius": 1.5 * mm});
            skCircle(sketch, "E9.20.2.0", {"center": v(123, 15) * mm, "radius": 1.5 * mm});
            skCircle(sketch, "E9.20.3.0", {"center": v(123, 21) * mm, "radius": 1.5 * mm});
            skCircle(sketch, "E9.20.4.0", {"center": v(123, 27) * mm, "radius": 1.5 * mm});
            skCircle(sketch, "E9.20.5.0", {"center": v(123, 33) * mm, "radius": 1.5 * mm});
            skCircle(sketch, "E9.20.6.0", {"center": v(123, 39) * mm, "radius": 1.5 * mm});
            skCircle(sketch, "E9.20.7.0", {"center": v(123, 45) * mm, "radius": 1.5 * mm});
            skCircle(sketch, "E9.20.8.0", {"center": v(123, 51) * mm, "radius": 1.5 * mm});
            skCircle(sketch, "E9.20.9.0", {"center": v(123, 57) * mm, "radius": 1.5 * mm});
            skCircle(sketch, "E9.20.10.0", {"center": v(123, 63) * mm, "radius": 1.5 * mm});
            skCircle(sketch, "E9.20.11.0", {"center": v(123, 69) * mm, "radius": 1.5 * mm});
            skCircle(sketch, "E9.20.12.0", {"center": v(123, 75) * mm, "radius": 1.5 * mm});
            skCircle(sketch, "E9.20.13.0", {"center": v(123, 81) * mm, "radius": 1.5 * mm});
            skCircle(sketch, "E9.20.14.0", {"center": v(123, 87) * mm, "radius": 1.5 * mm});
            skCircle(sketch, "E9.20.15.0", {"center": v(123, 93) * mm, "radius": 1.5 * mm});
            skCircle(sketch, "E9.21.0.0", {"center": v(129, 3) * mm, "radius": 1.5 * mm});
            skCircle(sketch, "E9.21.1.0", {"center": v(129, 9) * mm, "radius": 1.5 * mm});
            skCircle(sketch, "E9.21.2.0", {"center": v(129, 15) * mm, "radius": 1.5 * mm});
            skCircle(sketch, "E9.21.3.0", {"center": v(129, 21) * mm, "radius": 1.5 * mm});
            skCircle(sketch, "E9.21.4.0", {"center": v(129, 27) * mm, "radius": 1.5 * mm});
            skCircle(sketch, "E9.21.5.0", {"center": v(129, 33) * mm, "radius": 1.5 * mm});
            skCircle(sketch, "E9.21.6.0", {"center": v(129, 39) * mm, "radius": 1.5 * mm});
            skCircle(sketch, "E9.21.7.0", {"center": v(129, 45) * mm, "radius": 1.5 * mm});
            skCircle(sketch, "E9.21.8.0", {"center": v(129, 51) * mm, "radius": 1.5 * mm});
            skCircle(sketch, "E9.21.9.0", {"center": v(129, 57) * mm, "radius": 1.5 * mm});
            skCircle(sketch, "E9.21.10.0", {"center": v(129, 63) * mm, "radius": 1.5 * mm});
            skCircle(sketch, "E9.21.11.0", {"center": v(129, 69) * mm, "radius": 1.5 * mm});
            skCircle(sketch, "E9.21.12.0", {"center": v(129, 75) * mm, "radius": 1.5 * mm});
            skCircle(sketch, "E9.21.13.0", {"center": v(129, 81) * mm, "radius": 1.5 * mm});
            skCircle(sketch, "E9.21.14.0", {"center": v(129, 87) * mm, "radius": 1.5 * mm});
            skCircle(sketch, "E9.21.15.0", {"center": v(129, 93) * mm, "radius": 1.5 * mm});
            skCircle(sketch, "E9.22.0.0", {"center": v(135, 3) * mm, "radius": 1.5 * mm});
            skCircle(sketch, "E9.22.1.0", {"center": v(135, 9) * mm, "radius": 1.5 * mm});
            skCircle(sketch, "E9.22.2.0", {"center": v(135, 15) * mm, "radius": 1.5 * mm});
            skCircle(sketch, "E9.22.3.0", {"center": v(135, 21) * mm, "radius": 1.5 * mm});
            skCircle(sketch, "E9.22.4.0", {"center": v(135, 27) * mm, "radius": 1.5 * mm});
            skCircle(sketch, "E9.22.5.0", {"center": v(135, 33) * mm, "radius": 1.5 * mm});
            skCircle(sketch, "E9.22.6.0", {"center": v(135, 39) * mm, "radius": 1.5 * mm});
            skCircle(sketch, "E9.22.7.0", {"center": v(135, 45) * mm, "radius": 1.5 * mm});
            skCircle(sketch, "E9.22.8.0", {"center": v(135, 51) * mm, "radius": 1.5 * mm});
            skCircle(sketch, "E9.22.9.0", {"center": v(135, 57) * mm, "radius": 1.5 * mm});
            skCircle(sketch, "E9.22.10.0", {"center": v(135, 63) * mm, "radius": 1.5 * mm});
            skCircle(sketch, "E9.22.11.0", {"center": v(135, 69) * mm, "radius": 1.5 * mm});
            skCircle(sketch, "E9.22.12.0", {"center": v(135, 75) * mm, "radius": 1.5 * mm});
            skCircle(sketch, "E9.22.13.0", {"center": v(135, 81) * mm, "radius": 1.5 * mm});
            skCircle(sketch, "E9.22.14.0", {"center": v(135, 87) * mm, "radius": 1.5 * mm});
            skCircle(sketch, "E9.22.15.0", {"center": v(135, 93) * mm, "radius": 1.5 * mm});
            skCircle(sketch, "E9.23.0.0", {"center": v(141, 3) * mm, "radius": 1.5 * mm});
            skCircle(sketch, "E9.23.1.0", {"center": v(141, 9) * mm, "radius": 1.5 * mm});
            skCircle(sketch, "E9.23.2.0", {"center": v(141, 15) * mm, "radius": 1.5 * mm});
            skCircle(sketch, "E9.23.3.0", {"center": v(141, 21) * mm, "radius": 1.5 * mm});
            skCircle(sketch, "E9.23.4.0", {"center": v(141, 27) * mm, "radius": 1.5 * mm});
            skCircle(sketch, "E9.23.5.0", {"center": v(141, 33) * mm, "radius": 1.5 * mm});
            skCircle(sketch, "E9.23.6.0", {"center": v(141, 39) * mm, "radius": 1.5 * mm});
            skCircle(sketch, "E9.23.7.0", {"center": v(141, 45) * mm, "radius": 1.5 * mm});
            skCircle(sketch, "E9.23.8.0", {"center": v(141, 51) * mm, "radius": 1.5 * mm});
            skCircle(sketch, "E9.23.9.0", {"center": v(141, 57) * mm, "radius": 1.5 * mm});
            skCircle(sketch, "E9.23.10.0", {"center": v(141, 63) * mm, "radius": 1.5 * mm});
            skCircle(sketch, "E9.23.11.0", {"center": v(141, 69) * mm, "radius": 1.5 * mm});
            skCircle(sketch, "E9.23.12.0", {"center": v(141, 75) * mm, "radius": 1.5 * mm});
            skCircle(sketch, "E9.23.13.0", {"center": v(141, 81) * mm, "radius": 1.5 * mm});
            skCircle(sketch, "E9.23.14.0", {"center": v(141, 87) * mm, "radius": 1.5 * mm});
            skCircle(sketch, "E9.23.15.0", {"center": v(141, 93) * mm, "radius": 1.5 * mm});
            skCircle(sketch, "E9.24.0.0", {"center": v(147, 3) * mm, "radius": 1.5 * mm});
            skCircle(sketch, "E9.24.1.0", {"center": v(147, 9) * mm, "radius": 1.5 * mm});
            skCircle(sketch, "E9.24.2.0", {"center": v(147, 15) * mm, "radius": 1.5 * mm});
            skCircle(sketch, "E9.24.3.0", {"center": v(147, 21) * mm, "radius": 1.5 * mm});
            skCircle(sketch, "E9.24.4.0", {"center": v(147, 27) * mm, "radius": 1.5 * mm});
            skCircle(sketch, "E9.24.5.0", {"center": v(147, 33) * mm, "radius": 1.5 * mm});
            skCircle(sketch, "E9.24.6.0", {"center": v(147, 39) * mm, "radius": 1.5 * mm});
            skCircle(sketch, "E9.24.7.0", {"center": v(147, 45) * mm, "radius": 1.5 * mm});
            skCircle(sketch, "E9.24.8.0", {"center": v(147, 51) * mm, "radius": 1.5 * mm});
            skCircle(sketch, "E9.24.9.0", {"center": v(147, 57) * mm, "radius": 1.5 * mm});
            skCircle(sketch, "E9.24.10.0", {"center": v(147, 63) * mm, "radius": 1.5 * mm});
            skCircle(sketch, "E9.24.11.0", {"center": v(147, 69) * mm, "radius": 1.5 * mm});
            skCircle(sketch, "E9.24.12.0", {"center": v(147, 75) * mm, "radius": 1.5 * mm});
            skCircle(sketch, "E9.24.13.0", {"center": v(147, 81) * mm, "radius": 1.5 * mm});
            skCircle(sketch, "E9.24.14.0", {"center": v(147, 87) * mm, "radius": 1.5 * mm});
            skCircle(sketch, "E9.24.15.0", {"center": v(147, 93) * mm, "radius": 1.5 * mm});
            skCircle(sketch, "E9.25.0.0", {"center": v(153, 3) * mm, "radius": 1.5 * mm});
            skCircle(sketch, "E9.25.1.0", {"center": v(153, 9) * mm, "radius": 1.5 * mm});
            skCircle(sketch, "E9.25.2.0", {"center": v(153, 15) * mm, "radius": 1.5 * mm});
            skCircle(sketch, "E9.25.3.0", {"center": v(153, 21) * mm, "radius": 1.5 * mm});
            skCircle(sketch, "E9.25.4.0", {"center": v(153, 27) * mm, "radius": 1.5 * mm});
            skCircle(sketch, "E9.25.5.0", {"center": v(153, 33) * mm, "radius": 1.5 * mm});
            skCircle(sketch, "E9.25.6.0", {"center": v(153, 39) * mm, "radius": 1.5 * mm});
            skCircle(sketch, "E9.25.7.0", {"center": v(153, 45) * mm, "radius": 1.5 * mm});
            skCircle(sketch, "E9.25.8.0", {"center": v(153, 51) * mm, "radius": 1.5 * mm});
            skCircle(sketch, "E9.25.9.0", {"center": v(153, 57) * mm, "radius": 1.5 * mm});
            skCircle(sketch, "E9.25.10.0", {"center": v(153, 63) * mm, "radius": 1.5 * mm});
            skCircle(sketch, "E9.25.11.0", {"center": v(153, 69) * mm, "radius": 1.5 * mm});
            skCircle(sketch, "E9.25.12.0", {"center": v(153, 75) * mm, "radius": 1.5 * mm});
            skCircle(sketch, "E9.25.13.0", {"center": v(153, 81) * mm, "radius": 1.5 * mm});
            skCircle(sketch, "E9.25.14.0", {"center": v(153, 87) * mm, "radius": 1.5 * mm});
            skCircle(sketch, "E9.25.15.0", {"center": v(153, 93) * mm, "radius": 1.5 * mm});
            skCircle(sketch, "E9.26.0.0", {"center": v(159, 3) * mm, "radius": 1.5 * mm});
            skCircle(sketch, "E9.26.1.0", {"center": v(159, 9) * mm, "radius": 1.5 * mm});
            skCircle(sketch, "E9.26.2.0", {"center": v(159, 15) * mm, "radius": 1.5 * mm});
            skCircle(sketch, "E9.26.3.0", {"center": v(159, 21) * mm, "radius": 1.5 * mm});
            skCircle(sketch, "E9.26.4.0", {"center": v(159, 27) * mm, "radius": 1.5 * mm});
            skCircle(sketch, "E9.26.5.0", {"center": v(159, 33) * mm, "radius": 1.5 * mm});
            skCircle(sketch, "E9.26.6.0", {"center": v(159, 39) * mm, "radius": 1.5 * mm});
            skCircle(sketch, "E9.26.7.0", {"center": v(159, 45) * mm, "radius": 1.5 * mm});
            skCircle(sketch, "E9.26.8.0", {"center": v(159, 51) * mm, "radius": 1.5 * mm});
            skCircle(sketch, "E9.26.9.0", {"center": v(159, 57) * mm, "radius": 1.5 * mm});
            skCircle(sketch, "E9.26.10.0", {"center": v(159, 63) * mm, "radius": 1.5 * mm});
            skCircle(sketch, "E9.26.11.0", {"center": v(159, 69) * mm, "radius": 1.5 * mm});
            skCircle(sketch, "E9.26.12.0", {"center": v(159, 75) * mm, "radius": 1.5 * mm});
            skCircle(sketch, "E9.26.13.0", {"center": v(159, 81) * mm, "radius": 1.5 * mm});
            skCircle(sketch, "E9.26.14.0", {"center": v(159, 87) * mm, "radius": 1.5 * mm});
            skCircle(sketch, "E9.26.15.0", {"center": v(159, 93) * mm, "radius": 1.5 * mm});
            skCircle(sketch, "E9.27.0.0", {"center": v(165, 3) * mm, "radius": 1.5 * mm});
            skCircle(sketch, "E9.27.1.0", {"center": v(165, 9) * mm, "radius": 1.5 * mm});
            skCircle(sketch, "E9.27.2.0", {"center": v(165, 15) * mm, "radius": 1.5 * mm});
            skCircle(sketch, "E9.27.3.0", {"center": v(165, 21) * mm, "radius": 1.5 * mm});
            skCircle(sketch, "E9.27.4.0", {"center": v(165, 27) * mm, "radius": 1.5 * mm});
            skCircle(sketch, "E9.27.5.0", {"center": v(165, 33) * mm, "radius": 1.5 * mm});
            skCircle(sketch, "E9.27.6.0", {"center": v(165, 39) * mm, "radius": 1.5 * mm});
            skCircle(sketch, "E9.27.7.0", {"center": v(165, 45) * mm, "radius": 1.5 * mm});
            skCircle(sketch, "E9.27.8.0", {"center": v(165, 51) * mm, "radius": 1.5 * mm});
            skCircle(sketch, "E9.27.9.0", {"center": v(165, 57) * mm, "radius": 1.5 * mm});
            skCircle(sketch, "E9.27.10.0", {"center": v(165, 63) * mm, "radius": 1.5 * mm});
            skCircle(sketch, "E9.27.11.0", {"center": v(165, 69) * mm, "radius": 1.5 * mm});
            skCircle(sketch, "E9.27.12.0", {"center": v(165, 75) * mm, "radius": 1.5 * mm});
            skCircle(sketch, "E9.27.13.0", {"center": v(165, 81) * mm, "radius": 1.5 * mm});
            skCircle(sketch, "E9.27.14.0", {"center": v(165, 87) * mm, "radius": 1.5 * mm});
            skCircle(sketch, "E9.27.15.0", {"center": v(165, 93) * mm, "radius": 1.5 * mm});
            skCircle(sketch, "E9.28.0.0", {"center": v(171, 3) * mm, "radius": 1.5 * mm});
            skCircle(sketch, "E9.28.1.0", {"center": v(171, 9) * mm, "radius": 1.5 * mm});
            skCircle(sketch, "E9.28.2.0", {"center": v(171, 15) * mm, "radius": 1.5 * mm});
            skCircle(sketch, "E9.28.3.0", {"center": v(171, 21) * mm, "radius": 1.5 * mm});
            skCircle(sketch, "E9.28.4.0", {"center": v(171, 27) * mm, "radius": 1.5 * mm});
            skCircle(sketch, "E9.28.5.0", {"center": v(171, 33) * mm, "radius": 1.5 * mm});
            skCircle(sketch, "E9.28.6.0", {"center": v(171, 39) * mm, "radius": 1.5 * mm});
            skCircle(sketch, "E9.28.7.0", {"center": v(171, 45) * mm, "radius": 1.5 * mm});
            skCircle(sketch, "E9.28.8.0", {"center": v(171, 51) * mm, "radius": 1.5 * mm});
            skCircle(sketch, "E9.28.9.0", {"center": v(171, 57) * mm, "radius": 1.5 * mm});
            skCircle(sketch, "E9.28.10.0", {"center": v(171, 63) * mm, "radius": 1.5 * mm});
            skCircle(sketch, "E9.28.11.0", {"center": v(171, 69) * mm, "radius": 1.5 * mm});
            skCircle(sketch, "E9.28.12.0", {"center": v(171, 75) * mm, "radius": 1.5 * mm});
            skCircle(sketch, "E9.28.13.0", {"center": v(171, 81) * mm, "radius": 1.5 * mm});
            skCircle(sketch, "E9.28.14.0", {"center": v(171, 87) * mm, "radius": 1.5 * mm});
            skCircle(sketch, "E9.28.15.0", {"center": v(171, 93) * mm, "radius": 1.5 * mm});
            skCircle(sketch, "E9.29.0.0", {"center": v(177, 3) * mm, "radius": 1.5 * mm});
            skCircle(sketch, "E9.29.1.0", {"center": v(177, 9) * mm, "radius": 1.5 * mm});
            skCircle(sketch, "E9.29.2.0", {"center": v(177, 15) * mm, "radius": 1.5 * mm});
            skCircle(sketch, "E9.29.3.0", {"center": v(177, 21) * mm, "radius": 1.5 * mm});
            skCircle(sketch, "E9.29.4.0", {"center": v(177, 27) * mm, "radius": 1.5 * mm});
            skCircle(sketch, "E9.29.5.0", {"center": v(177, 33) * mm, "radius": 1.5 * mm});
            skCircle(sketch, "E9.29.6.0", {"center": v(177, 39) * mm, "radius": 1.5 * mm});
            skCircle(sketch, "E9.29.7.0", {"center": v(177, 45) * mm, "radius": 1.5 * mm});
            skCircle(sketch, "E9.29.8.0", {"center": v(177, 51) * mm, "radius": 1.5 * mm});
            skCircle(sketch, "E9.29.9.0", {"center": v(177, 57) * mm, "radius": 1.5 * mm});
            skCircle(sketch, "E9.29.10.0", {"center": v(177, 63) * mm, "radius": 1.5 * mm});
            skCircle(sketch, "E9.29.11.0", {"center": v(177, 69) * mm, "radius": 1.5 * mm});
            skCircle(sketch, "E9.29.12.0", {"center": v(177, 75) * mm, "radius": 1.5 * mm});
            skCircle(sketch, "E9.29.13.0", {"center": v(177, 81) * mm, "radius": 1.5 * mm});
            skCircle(sketch, "E9.29.14.0", {"center": v(177, 87) * mm, "radius": 1.5 * mm});
            skCircle(sketch, "E9.29.15.0", {"center": v(177, 93) * mm, "radius": 1.5 * mm});
            skCircle(sketch, "E9.30.0.0", {"center": v(183, 3) * mm, "radius": 1.5 * mm});
            skCircle(sketch, "E9.30.1.0", {"center": v(183, 9) * mm, "radius": 1.5 * mm});
            skCircle(sketch, "E9.30.2.0", {"center": v(183, 15) * mm, "radius": 1.5 * mm});
            skCircle(sketch, "E9.30.3.0", {"center": v(183, 21) * mm, "radius": 1.5 * mm});
            skCircle(sketch, "E9.30.4.0", {"center": v(183, 27) * mm, "radius": 1.5 * mm});
            skCircle(sketch, "E9.30.5.0", {"center": v(183, 33) * mm, "radius": 1.5 * mm});
            skCircle(sketch, "E9.30.6.0", {"center": v(183, 39) * mm, "radius": 1.5 * mm});
            skCircle(sketch, "E9.30.7.0", {"center": v(183, 45) * mm, "radius": 1.5 * mm});
            skCircle(sketch, "E9.30.8.0", {"center": v(183, 51) * mm, "radius": 1.5 * mm});
            skCircle(sketch, "E9.30.9.0", {"center": v(183, 57) * mm, "radius": 1.5 * mm});
            skCircle(sketch, "E9.30.10.0", {"center": v(183, 63) * mm, "radius": 1.5 * mm});
            skCircle(sketch, "E9.30.11.0", {"center": v(183, 69) * mm, "radius": 1.5 * mm});
            skCircle(sketch, "E9.30.12.0", {"center": v(183, 75) * mm, "radius": 1.5 * mm});
            skCircle(sketch, "E9.30.13.0", {"center": v(183, 81) * mm, "radius": 1.5 * mm});
            skCircle(sketch, "E9.30.14.0", {"center": v(183, 87) * mm, "radius": 1.5 * mm});
            skCircle(sketch, "E9.30.15.0", {"center": v(183, 93) * mm, "radius": 1.5 * mm});
            skCircle(sketch, "E9.31.0.0", {"center": v(189, 3) * mm, "radius": 1.5 * mm});
            skCircle(sketch, "E9.31.1.0", {"center": v(189, 9) * mm, "radius": 1.5 * mm});
            skCircle(sketch, "E9.31.2.0", {"center": v(189, 15) * mm, "radius": 1.5 * mm});
            skCircle(sketch, "E9.31.3.0", {"center": v(189, 21) * mm, "radius": 1.5 * mm});
            skCircle(sketch, "E9.31.4.0", {"center": v(189, 27) * mm, "radius": 1.5 * mm});
            skCircle(sketch, "E9.31.5.0", {"center": v(189, 33) * mm, "radius": 1.5 * mm});
            skCircle(sketch, "E9.31.6.0", {"center": v(189, 39) * mm, "radius": 1.5 * mm});
            skCircle(sketch, "E9.31.7.0", {"center": v(189, 45) * mm, "radius": 1.5 * mm});
            skCircle(sketch, "E9.31.8.0", {"center": v(189, 51) * mm, "radius": 1.5 * mm});
            skCircle(sketch, "E9.31.9.0", {"center": v(189, 57) * mm, "radius": 1.5 * mm});
            skCircle(sketch, "E9.31.10.0", {"center": v(189, 63) * mm, "radius": 1.5 * mm});
            skCircle(sketch, "E9.31.11.0", {"center": v(189, 69) * mm, "radius": 1.5 * mm});
            skCircle(sketch, "E9.31.12.0", {"center": v(189, 75) * mm, "radius": 1.5 * mm});
            skCircle(sketch, "E9.31.13.0", {"center": v(189, 81) * mm, "radius": 1.5 * mm});
            skCircle(sketch, "E9.31.14.0", {"center": v(189, 87) * mm, "radius": 1.5 * mm});
            skCircle(sketch, "E9.31.15.0", {"center": v(189, 93) * mm, "radius": 1.5 * mm});
            skLineSegment(sketch, "E9.direction1", {"start": v(3, 3) * mm, "end": v(9, 3) * mm, "construction": true});
            skLineSegment(sketch, "E9.direction2", {"start": v(3, 3) * mm, "end": v(3, 9) * mm, "construction": true});
            skSolve(sketch);
        }
        {
            var Q0;
            Q0 = qSketchRegion(id + "F7", true);
            extrude(context, id + "F8", {"entities" : qUnion([Q0]), "operationType" : NewBodyOperationType.REMOVE, "oppositeDirection" : true, "depth" : 2 * mm});
        }
    });
